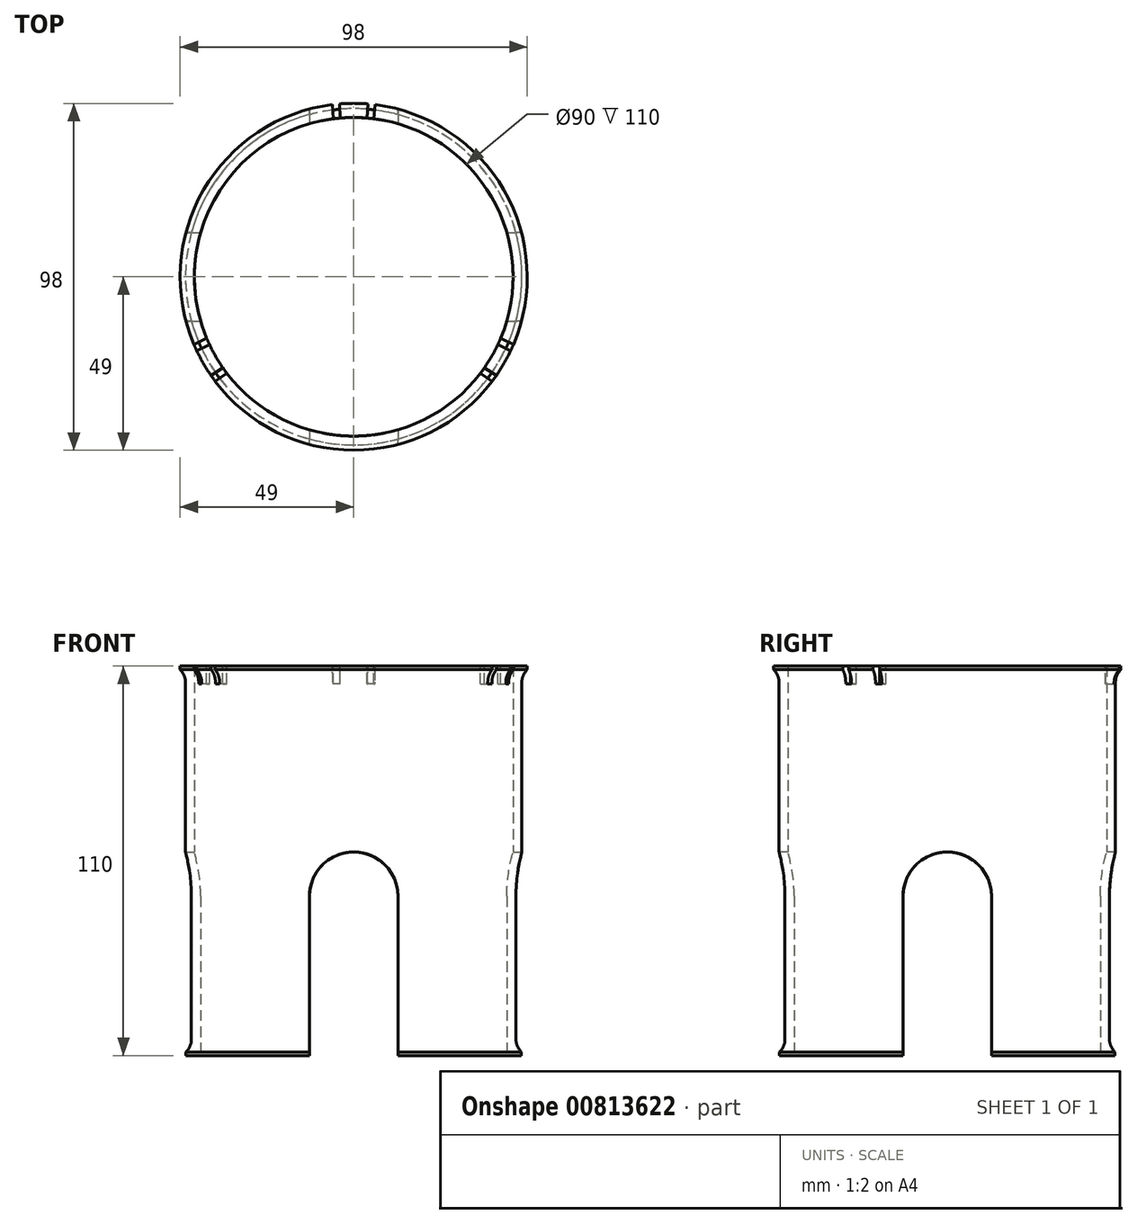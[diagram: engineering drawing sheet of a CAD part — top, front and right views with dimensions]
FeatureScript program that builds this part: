
annotation { "Feature Type Name" : "Feature", "Feature Type Description" : "" }
export const myFeature = defineFeature(function(context is Context, id is Id, definition is map)
    precondition{}
    {
        {
            var Q0;
            Q0=qCreatedBy(makeId("Top.planeOp"),FACE);
            var sketch = newSketch(context, id + "F0", { "sketchPlane" : qUnion([Q0])});
            skCircle(sketch, "E0", {"center": v(0, 0) * mm, "radius": 45 * mm});
            skCircle(sketch, "E1", {"center": v(0, 0) * mm, "radius": 47.5 * mm});
            skSolve(sketch);
        }
        {
            var Q0;
            Q0 = qSketchRegion(id + "F0", true);
            extrude(context, id + "F1", {"entities" : qUnion([Q0]), "depth" : 110 * mm, "offsetDistance" : 25 * mm});
        }
        {
            var Q0;
            Q0=qCreatedBy(makeId("Top.planeOp"),FACE);
            var sketch = newSketch(context, id + "F2", { "sketchPlane" : qUnion([Q0])});
            skCircle(sketch, "E2", {"center": v(0, 0) * mm, "radius": 45 * mm});
            skCircle(sketch, "E3", {"center": v(0, 0) * mm, "radius": 49 * mm});
            skSolve(sketch);
        }
        {
            var Q0;
            Q0 = qSketchRegion(id + "F2", true);
            extrude(context, id + "F3", {"entities" : qUnion([Q0]), "operationType" : NewBodyOperationType.ADD, "depth" : 1 * mm, "offsetDistance" : 25 * mm});
        }
        {
            var Q0;
            {var subQ0=makeQuery(id+"F1.opExtrude","SWEPT_FACE",FACE,{"disambiguationData":[OSD([sQuery(id+"F0.wireOp",EDGE,"E1")])]});var subQ1=makeQuery(id+"F3.opExtrude","CAP_FACE",FACE,{"disambiguationData":[OSD([sQuery(id+"F2.wireOp",EDGE,"E2"),sQuery(id+"F2.wireOp",EDGE,"E3")])],"isStart":false});var subQ2=makeQuery(id+"F6.opExtrude","SWEPT_FACE",FACE,{"disambiguationData":[OSD([sQuery(id+"F5.wireOp",EDGE,"E4.left")])]});Q0=makeQuery(id+"F8.boolean.opBoolean","SPLIT",EDGE,{"disambiguationData":[TD([makeQuery(id+"F6.boolean.opBoolean","COPY",FACE,{"disambiguationData":[OD(1.0)],"derivedFrom":subQ2})])],"derivedFrom":makeQuery(id+"F6.boolean.opBoolean","SPLIT",EDGE,{"disambiguationData":[TD([subQ2])],"derivedFrom":makeQuery(id+"F3.boolean.opBoolean","INTERSECT",EDGE,{"derivedFrom":[subQ0,subQ1]})})});}
            var Q1;
            {var subQ0=makeQuery(id+"F1.opExtrude","SWEPT_FACE",FACE,{"disambiguationData":[OSD([sQuery(id+"F0.wireOp",EDGE,"E1")])]});var subQ1=makeQuery(id+"F3.opExtrude","CAP_FACE",FACE,{"disambiguationData":[OSD([sQuery(id+"F2.wireOp",EDGE,"E2"),sQuery(id+"F2.wireOp",EDGE,"E3")])],"isStart":false});var subQ2=makeQuery(id+"F6.opExtrude","SWEPT_FACE",FACE,{"disambiguationData":[OSD([sQuery(id+"F5.wireOp",EDGE,"E4.right")])]});Q1=makeQuery(id+"F8.boolean.opBoolean","SPLIT",EDGE,{"disambiguationData":[TD([makeQuery(id+"F6.boolean.opBoolean","COPY",FACE,{"disambiguationData":[OD(1.0)],"derivedFrom":subQ2})])],"derivedFrom":makeQuery(id+"F6.boolean.opBoolean","SPLIT",EDGE,{"disambiguationData":[TD([subQ2])],"derivedFrom":makeQuery(id+"F3.boolean.opBoolean","INTERSECT",EDGE,{"derivedFrom":[subQ0,subQ1]})})});}
            var Q2;
            {var subQ0=makeQuery(id+"F1.opExtrude","SWEPT_FACE",FACE,{"disambiguationData":[OSD([sQuery(id+"F0.wireOp",EDGE,"E1")])]});var subQ1=makeQuery(id+"F3.opExtrude","CAP_FACE",FACE,{"disambiguationData":[OSD([sQuery(id+"F2.wireOp",EDGE,"E2"),sQuery(id+"F2.wireOp",EDGE,"E3")])],"isStart":false});var subQ2=makeQuery(id+"F6.opExtrude","SWEPT_FACE",FACE,{"disambiguationData":[OSD([sQuery(id+"F5.wireOp",EDGE,"E4.left")])]});Q2=makeQuery(id+"F8.boolean.opBoolean","SPLIT",EDGE,{"disambiguationData":[TD([makeQuery(id+"F6.boolean.opBoolean","COPY",FACE,{"disambiguationData":[OD(0.0)],"derivedFrom":subQ2})])],"derivedFrom":makeQuery(id+"F6.boolean.opBoolean","SPLIT",EDGE,{"disambiguationData":[TD([subQ2])],"derivedFrom":makeQuery(id+"F3.boolean.opBoolean","INTERSECT",EDGE,{"derivedFrom":[subQ0,subQ1]})})});}
            var Q3;
            {var subQ0=makeQuery(id+"F1.opExtrude","SWEPT_FACE",FACE,{"disambiguationData":[OSD([sQuery(id+"F0.wireOp",EDGE,"E1")])]});var subQ1=makeQuery(id+"F6.opExtrude","SWEPT_FACE",FACE,{"disambiguationData":[OSD([sQuery(id+"F5.wireOp",EDGE,"E4.right")])]});var subQ2=makeQuery(id+"F3.opExtrude","CAP_FACE",FACE,{"disambiguationData":[OSD([sQuery(id+"F2.wireOp",EDGE,"E2"),sQuery(id+"F2.wireOp",EDGE,"E3")])],"isStart":false});Q3=makeQuery(id+"F8.boolean.opBoolean","SPLIT",EDGE,{"disambiguationData":[TD([makeQuery(id+"F6.boolean.opBoolean","COPY",FACE,{"disambiguationData":[OD(0.0)],"derivedFrom":subQ1})])],"derivedFrom":makeQuery(id+"F6.boolean.opBoolean","SPLIT",EDGE,{"disambiguationData":[TD([subQ1])],"derivedFrom":makeQuery(id+"F3.boolean.opBoolean","INTERSECT",EDGE,{"derivedFrom":[subQ0,subQ2]})})});}
            fillet(context, id + "F4", {"entities" : qUnion([Q0, Q1, Q2, Q3]), "radius" : 5 * mm, "tangentPropagation" : true, "allowEdgeOverflow" : false});
        }
        {
            var Q0;
            Q0=qCreatedBy(makeId("Right.planeOp"),FACE);
            var sketch = newSketch(context, id + "F5", { "sketchPlane" : qUnion([Q0])});
            skLineSegment(sketch, "E4.top", {"start": v(12.5, -45) * mm, "end": v(-12.5, -45) * mm});
            skLineSegment(sketch, "E4.left", {"start": v(12.5, 45) * mm, "end": v(12.5, -45) * mm});
            skLineSegment(sketch, "E4.right", {"start": v(-12.5, 45) * mm, "end": v(-12.5, -45) * mm});
            skPoint(sketch, "E4.middle", {"position": v(0, 0) * mm});
            skArc(sketch, "E5", {"start": v(12.5, 45) * mm, "mid": v(0, 57.5) * mm, "end": v(-12.5, 45) * mm});
            skSolve(sketch);
        }
        {
            var Q0;
            Q0 = qSketchRegion(id + "F5", true);
            extrude(context, id + "F6", {"entities" : qUnion([Q0]), "operationType" : NewBodyOperationType.REMOVE, "endBound" : BoundingType.THROUGH_ALL, "oppositeDirection" : true, "depth" : 25 * mm, "offsetDistance" : 25 * mm, "hasSecondDirection" : true, "secondDirectionBound" : SecondDirectionBoundingType.THROUGH_ALL, "secondDirectionOppositeDirection" : false, "secondDirectionDepth" : 99 * mm});
        }
        {
            var Q0;
            Q0=qCreatedBy(makeId("Front.planeOp"),FACE);
            var sketch = newSketch(context, id + "F7", { "sketchPlane" : qUnion([Q0])});
            skLineSegment(sketch, "E6.top", {"start": v(12.5, -45) * mm, "end": v(-12.5, -45) * mm});
            skLineSegment(sketch, "E6.left", {"start": v(12.5, 45) * mm, "end": v(12.5, -45) * mm});
            skLineSegment(sketch, "E6.right", {"start": v(-12.5, 45) * mm, "end": v(-12.5, -45) * mm});
            skPoint(sketch, "E6.middle", {"position": v(0, 0) * mm});
            skArc(sketch, "E7", {"start": v(12.5, 45) * mm, "mid": v(0, 57.5) * mm, "end": v(-12.5, 45) * mm});
            skSolve(sketch);
        }
        {
            var Q0;
            Q0 = qSketchRegion(id + "F7", true);
            extrude(context, id + "F8", {"entities" : qUnion([Q0]), "operationType" : NewBodyOperationType.REMOVE, "endBound" : BoundingType.THROUGH_ALL, "oppositeDirection" : true, "depth" : 25 * mm, "offsetDistance" : 25 * mm, "hasSecondDirection" : true, "secondDirectionBound" : SecondDirectionBoundingType.THROUGH_ALL, "secondDirectionOppositeDirection" : false, "secondDirectionDepth" : 25 * mm});
        }
        {
            var Q0;
            {var subQ0=sQuery(id+"F0.wireOp",EDGE,"E0");var subQ1=sQuery(id+"F0.wireOp",EDGE,"E1");Q0=makeQuery(id+"F12.boolean.opBoolean","SPLIT",FACE,{"disambiguationData":[TD([makeQuery(id+"F12.opExtrude","SWEPT_FACE",FACE,{"disambiguationData":[OSD([sQuery(id+"F11.wireOp",EDGE,"E19.1.7")])]})])],"derivedFrom":makeQuery(id+"F1.opExtrude","CAP_FACE",FACE,{"disambiguationData":[OSD([subQ0,subQ1])],"isStart":false})});}
            var sketch = newSketch(context, id + "F9", { "sketchPlane" : qUnion([Q0])});
            skCircle(sketch, "E8", {"center": v(0, 0) * mm, "radius": 49 * mm});
            skCircle(sketch, "E9", {"center": v(0, 0) * mm, "radius": 45 * mm});
            skSolve(sketch);
        }
        {
            var Q0;
            Q0 = qSketchRegion(id + "F9", true);
            extrude(context, id + "F10", {"entities" : qUnion([Q0]), "operationType" : NewBodyOperationType.ADD, "oppositeDirection" : true, "depth" : 1 * mm, "offsetDistance" : 25 * mm});
        }
        {
            var Q0;
            Q0=makeQuery(id+"F1.opExtrude","CAP_FACE",FACE,{"disambiguationData":[OSD([sQuery(id+"F0.wireOp",EDGE,"E0"),sQuery(id+"F0.wireOp",EDGE,"E1")])],"isStart":false});
            var sketch = newSketch(context, id + "F11", { "sketchPlane" : qUnion([Q0])});
            skPoint(sketch, "E10.center", {"position": v(0, 0) * mm});
            skLineSegment(sketch, "E11", {"start": v(-3.79, 44.84) * mm, "end": v(-4, 48.92) * mm});
            skLineSegment(sketch, "E12", {"start": v(3.79, 44.84) * mm, "end": v(4, 48.92) * mm});
            skLineSegment(sketch, "E13", {"start": v(5.74, 44.63) * mm, "end": v(6, 48.71) * mm});
            skLineSegment(sketch, "E14", {"start": v(-5.74, 44.63) * mm, "end": v(-6, 48.71) * mm});
            skArc(sketch, "E15.0", {"start": v(6, 48.71) * mm, "mid": v(5, 48.83) * mm, "end": v(4, 48.92) * mm});
            skArc(sketch, "E16.0", {"start": v(5.74, 44.63) * mm, "mid": v(4.76, 44.75) * mm, "end": v(3.79, 44.84) * mm});
            skArc(sketch, "E17.trimOffspring", {"start": v(-3.79, 44.84) * mm, "mid": v(-4.76, 44.75) * mm, "end": v(-5.74, 44.63) * mm});
            skArc(sketch, "E18.trimOffspring", {"start": v(-4, 48.92) * mm, "mid": v(-5, 48.83) * mm, "end": v(-6, 48.71) * mm});
            skArc(sketch, "E19.1.0", {"start": v(-36.94, -25.7) * mm, "mid": v(-36.37, -26.5) * mm, "end": v(-35.78, -27.28) * mm});
            skArc(sketch, "E19.1.1", {"start": v(-41.52, -17.35) * mm, "mid": v(-41.13, -18.25) * mm, "end": v(-40.73, -19.14) * mm});
            skLineSegment(sketch, "E19.1.2", {"start": v(-41.52, -17.35) * mm, "end": v(-45.19, -19.16) * mm});
            skLineSegment(sketch, "E19.1.3", {"start": v(-40.73, -19.14) * mm, "end": v(-44.36, -21) * mm});
            skLineSegment(sketch, "E19.1.4", {"start": v(-36.94, -25.7) * mm, "end": v(-40.36, -27.92) * mm});
            skArc(sketch, "E19.1.5", {"start": v(-40.36, -27.92) * mm, "mid": v(-39.78, -28.74) * mm, "end": v(-39.19, -29.55) * mm});
            skArc(sketch, "E19.1.6", {"start": v(-45.19, -19.16) * mm, "mid": v(-44.79, -20.08) * mm, "end": v(-44.36, -21) * mm});
            skLineSegment(sketch, "E19.1.7", {"start": v(-35.78, -27.28) * mm, "end": v(-39.19, -29.55) * mm});
            skArc(sketch, "E19.2.0", {"start": v(40.73, -19.14) * mm, "mid": v(41.13, -18.25) * mm, "end": v(41.52, -17.35) * mm});
            skArc(sketch, "E19.2.1", {"start": v(35.78, -27.28) * mm, "mid": v(36.37, -26.5) * mm, "end": v(36.94, -25.7) * mm});
            skLineSegment(sketch, "E19.2.2", {"start": v(35.78, -27.28) * mm, "end": v(39.19, -29.55) * mm});
            skLineSegment(sketch, "E19.2.3", {"start": v(36.94, -25.7) * mm, "end": v(40.36, -27.92) * mm});
            skLineSegment(sketch, "E19.2.4", {"start": v(40.73, -19.14) * mm, "end": v(44.36, -21) * mm});
            skArc(sketch, "E19.2.5", {"start": v(44.36, -21) * mm, "mid": v(44.79, -20.08) * mm, "end": v(45.19, -19.16) * mm});
            skArc(sketch, "E19.2.6", {"start": v(39.19, -29.55) * mm, "mid": v(39.78, -28.74) * mm, "end": v(40.36, -27.92) * mm});
            skLineSegment(sketch, "E19.2.7", {"start": v(41.52, -17.35) * mm, "end": v(45.19, -19.16) * mm});
            skSolve(sketch);
        }
        {
            var Q0;
            Q0 = qSketchRegion(id + "F11", true);
            extrude(context, id + "F12", {"entities" : qUnion([Q0]), "operationType" : NewBodyOperationType.REMOVE, "oppositeDirection" : true, "depth" : 5 * mm, "offsetDistance" : 25 * mm});
        }
        {
            var Q0;
            {var subQ0=makeQuery(id+"F1.opExtrude","SWEPT_FACE",FACE,{"disambiguationData":[OSD([sQuery(id+"F0.wireOp",EDGE,"E1")])]});var subQ1=makeQuery(id+"F10.opExtrude","CAP_FACE",FACE,{"disambiguationData":[OSD([sQuery(id+"F9.wireOp",EDGE,"E8"),sQuery(id+"F9.wireOp",EDGE,"E9")])],"isStart":false});Q0=makeQuery(id+"F12.boolean.opBoolean","SPLIT",EDGE,{"disambiguationData":[TD([makeQuery(id+"F12.opExtrude","SWEPT_FACE",FACE,{"disambiguationData":[OSD([sQuery(id+"F11.wireOp",EDGE,"E13")])]})])],"derivedFrom":makeQuery(id+"F10.boolean.opBoolean","INTERSECT",EDGE,{"derivedFrom":[subQ0,subQ1]})});}
            var Q1;
            {var subQ0=makeQuery(id+"F1.opExtrude","SWEPT_FACE",FACE,{"disambiguationData":[OSD([sQuery(id+"F0.wireOp",EDGE,"E1")])]});var subQ1=makeQuery(id+"F10.opExtrude","CAP_FACE",FACE,{"disambiguationData":[OSD([sQuery(id+"F9.wireOp",EDGE,"E8"),sQuery(id+"F9.wireOp",EDGE,"E9")])],"isStart":false});Q1=makeQuery(id+"F12.boolean.opBoolean","SPLIT",EDGE,{"disambiguationData":[TD([makeQuery(id+"F12.opExtrude","SWEPT_FACE",FACE,{"disambiguationData":[OSD([sQuery(id+"F11.wireOp",EDGE,"E19.1.7")])]})])],"derivedFrom":makeQuery(id+"F10.boolean.opBoolean","INTERSECT",EDGE,{"derivedFrom":[subQ0,subQ1]})});}
            var Q2;
            {var subQ0=makeQuery(id+"F1.opExtrude","SWEPT_FACE",FACE,{"disambiguationData":[OSD([sQuery(id+"F0.wireOp",EDGE,"E1")])]});var subQ1=makeQuery(id+"F10.opExtrude","CAP_FACE",FACE,{"disambiguationData":[OSD([sQuery(id+"F9.wireOp",EDGE,"E8"),sQuery(id+"F9.wireOp",EDGE,"E9")])],"isStart":false});Q2=makeQuery(id+"F12.boolean.opBoolean","SPLIT",EDGE,{"disambiguationData":[TD([makeQuery(id+"F12.opExtrude","SWEPT_FACE",FACE,{"disambiguationData":[OSD([sQuery(id+"F11.wireOp",EDGE,"E19.2.3")])]})])],"derivedFrom":makeQuery(id+"F10.boolean.opBoolean","INTERSECT",EDGE,{"derivedFrom":[subQ0,subQ1]})});}
            var Q3;
            {var subQ0=makeQuery(id+"F1.opExtrude","SWEPT_FACE",FACE,{"disambiguationData":[OSD([sQuery(id+"F0.wireOp",EDGE,"E1")])]});var subQ1=makeQuery(id+"F10.opExtrude","CAP_FACE",FACE,{"disambiguationData":[OSD([sQuery(id+"F9.wireOp",EDGE,"E8"),sQuery(id+"F9.wireOp",EDGE,"E9")])],"isStart":false});Q3=makeQuery(id+"F12.boolean.opBoolean","SPLIT",EDGE,{"disambiguationData":[TD([makeQuery(id+"F12.opExtrude","SWEPT_FACE",FACE,{"disambiguationData":[OSD([sQuery(id+"F11.wireOp",EDGE,"E19.1.3")])]})])],"derivedFrom":makeQuery(id+"F10.boolean.opBoolean","INTERSECT",EDGE,{"derivedFrom":[subQ0,subQ1]})});}
            var Q4;
            {var subQ0=makeQuery(id+"F1.opExtrude","SWEPT_FACE",FACE,{"disambiguationData":[OSD([sQuery(id+"F0.wireOp",EDGE,"E1")])]});var subQ1=makeQuery(id+"F10.opExtrude","CAP_FACE",FACE,{"disambiguationData":[OSD([sQuery(id+"F9.wireOp",EDGE,"E8"),sQuery(id+"F9.wireOp",EDGE,"E9")])],"isStart":false});Q4=makeQuery(id+"F12.boolean.opBoolean","SPLIT",EDGE,{"disambiguationData":[TD([makeQuery(id+"F12.opExtrude","SWEPT_FACE",FACE,{"disambiguationData":[OSD([sQuery(id+"F11.wireOp",EDGE,"E14")])]})])],"derivedFrom":makeQuery(id+"F10.boolean.opBoolean","INTERSECT",EDGE,{"derivedFrom":[subQ0,subQ1]})});}
            var Q5;
            {var subQ0=makeQuery(id+"F1.opExtrude","SWEPT_FACE",FACE,{"disambiguationData":[OSD([sQuery(id+"F0.wireOp",EDGE,"E1")])]});var subQ1=makeQuery(id+"F10.opExtrude","CAP_FACE",FACE,{"disambiguationData":[OSD([sQuery(id+"F9.wireOp",EDGE,"E8"),sQuery(id+"F9.wireOp",EDGE,"E9")])],"isStart":false});Q5=makeQuery(id+"F12.boolean.opBoolean","SPLIT",EDGE,{"disambiguationData":[TD([makeQuery(id+"F12.opExtrude","SWEPT_FACE",FACE,{"disambiguationData":[OSD([sQuery(id+"F11.wireOp",EDGE,"E11")])]})])],"derivedFrom":makeQuery(id+"F10.boolean.opBoolean","INTERSECT",EDGE,{"derivedFrom":[subQ0,subQ1]})});}
            fillet(context, id + "F13", {"entities" : qUnion([Q0, Q1, Q2, Q3, Q4, Q5]), "radius" : 5 * mm, "tangentPropagation" : true, "allowEdgeOverflow" : false});
        }
    });
